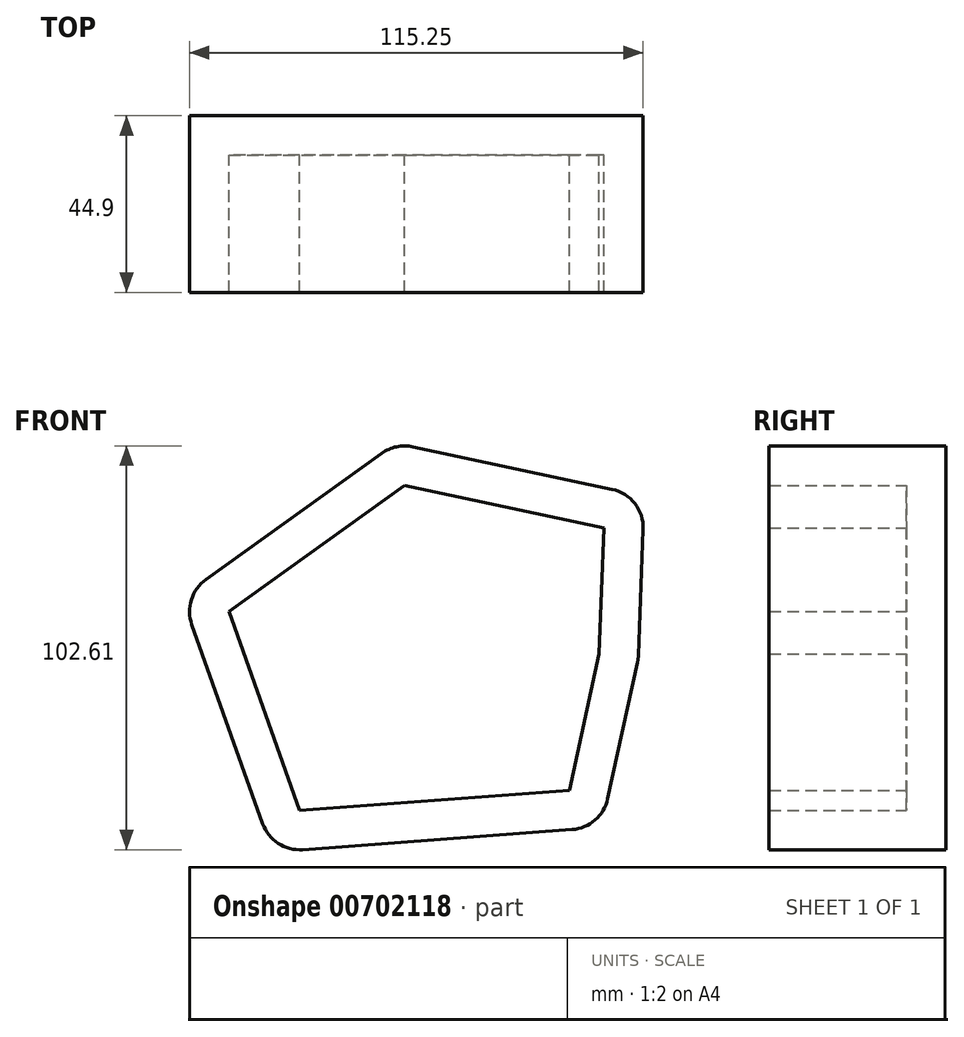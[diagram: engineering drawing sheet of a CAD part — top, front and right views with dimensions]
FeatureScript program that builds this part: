
annotation { "Feature Type Name" : "Feature", "Feature Type Description" : "" }
export const myFeature = defineFeature(function(context is Context, id is Id, definition is map)
    precondition{}
    {
        {
            var Q0;
            Q0=qCreatedBy(makeId("Front.planeOp"),FACE);
            var sketch = newSketch(context, id + "F0", { "sketchPlane" : qUnion([Q0])});
            skLineSegment(sketch, "E0", {"start": v(-55.51, 20.23) * mm, "end": v(-10.86, 52.28) * mm});
            skLineSegment(sketch, "E1", {"start": v(-2.95, 53.94) * mm, "end": v(47.65, 43.15) * mm});
            skLineSegment(sketch, "E2", {"start": v(55.56, 32.99) * mm, "end": v(54.33, 0.89) * mm});
            skLineSegment(sketch, "E3", {"start": v(54.11, -0.87) * mm, "end": v(46.55, -35.48) * mm});
            skLineSegment(sketch, "E4", {"start": v(37.53, -43.32) * mm, "end": v(-30.94, -48.42) * mm});
            skLineSegment(sketch, "E5", {"start": v(-41.1, -41.8) * mm, "end": v(-59.1, 8.75) * mm});
            skPoint(sketch, "E6.visualSharp", {"position": v(-7.27, 54.86) * mm});
            skArc(sketch, "E6.filletArc", {"start": v(-2.95, 53.94) * mm, "mid": v(-7.08, 53.94) * mm, "end": v(-10.86, 52.28) * mm});
            skPoint(sketch, "E7.visualSharp", {"position": v(55.88, 41.4) * mm});
            skArc(sketch, "E7.filletArc", {"start": v(55.56, 32.99) * mm, "mid": v(53.46, 39.5) * mm, "end": v(47.65, 43.15) * mm});
            skPoint(sketch, "E8.visualSharp", {"position": v(54.3, 0) * mm});
            skArc(sketch, "E8.filletArc", {"start": v(54.11, -0.87) * mm, "mid": v(54.26, 0) * mm, "end": v(54.33, 0.89) * mm});
            skPoint(sketch, "E9.visualSharp", {"position": v(44.96, -42.76) * mm});
            skArc(sketch, "E9.filletArc", {"start": v(37.53, -43.32) * mm, "mid": v(43.34, -40.9) * mm, "end": v(46.55, -35.48) * mm});
            skPoint(sketch, "E10.visualSharp", {"position": v(-38.55, -48.99) * mm});
            skArc(sketch, "E10.filletArc", {"start": v(-41.1, -41.8) * mm, "mid": v(-37.14, -46.83) * mm, "end": v(-30.94, -48.42) * mm});
            skPoint(sketch, "E11.visualSharp", {"position": v(-61.63, 15.84) * mm});
            skArc(sketch, "E11.filletArc", {"start": v(-55.51, 20.23) * mm, "mid": v(-59.23, 15.1) * mm, "end": v(-59.1, 8.75) * mm});
            skSolve(sketch);
        }
        {
            var Q0;
            Q0 = qSketchRegion(id + "F0", true);
            extrude(context, id + "F1", {"entities" : qUnion([Q0]), "depth" : 44.9 * mm, "offsetDistance" : 25 * mm});
        }
        {
            var Q0;
            Q0=makeQuery(id+"F1.opExtrude","CAP_FACE",FACE,{"disambiguationData":[OSD([sQuery(id+"F0.wireOp",EDGE,"E0"),sQuery(id+"F0.wireOp",EDGE,"E1"),sQuery(id+"F0.wireOp",EDGE,"E2"),sQuery(id+"F0.wireOp",EDGE,"E3"),sQuery(id+"F0.wireOp",EDGE,"E4"),sQuery(id+"F0.wireOp",EDGE,"E5"),sQuery(id+"F0.wireOp",EDGE,"E6.filletArc"),sQuery(id+"F0.wireOp",EDGE,"E7.filletArc"),sQuery(id+"F0.wireOp",EDGE,"E8.filletArc"),sQuery(id+"F0.wireOp",EDGE,"E9.filletArc"),sQuery(id+"F0.wireOp",EDGE,"E10.filletArc"),sQuery(id+"F0.wireOp",EDGE,"E11.filletArc")])],"isStart":false});
            shell(context, id + "F2", {"entities" : qUnion([Q0]), "thickness" : 10 * mm});
        }
    });
